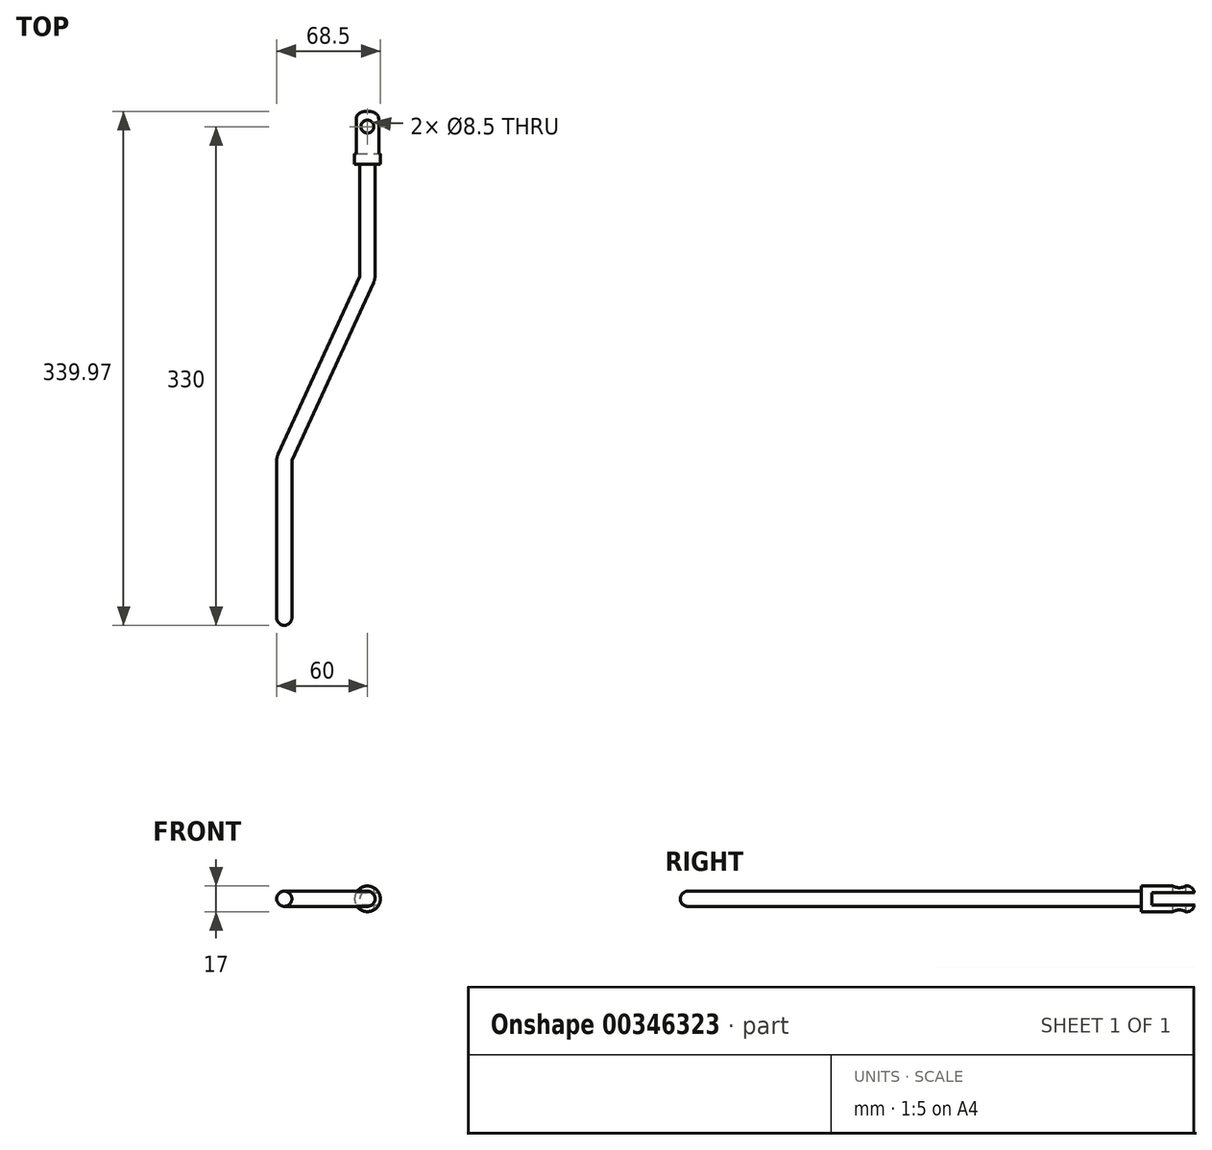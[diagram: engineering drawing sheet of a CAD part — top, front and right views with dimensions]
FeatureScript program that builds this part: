
annotation { "Feature Type Name" : "Feature", "Feature Type Description" : "" }
export const myFeature = defineFeature(function(context is Context, id is Id, definition is map)
    precondition{}
    {
        {
            var Q0;
            Q0=qCreatedBy(makeId("Top.planeOp"),FACE);
            var sketch = newSketch(context, id + "F0", { "sketchPlane" : qUnion([Q0])});
            skLineSegment(sketch, "E0.bottom", {"start": v(-3.5, 0) * mm, "end": v(3.5, 0) * mm});
            skLineSegment(sketch, "E0.top", {"start": v(-8.5, -35) * mm, "end": v(8.5, -35) * mm});
            skLineSegment(sketch, "E0.left", {"start": v(-8.5, -5) * mm, "end": v(-8.5, -35) * mm});
            skLineSegment(sketch, "E0.right", {"start": v(8.5, -5) * mm, "end": v(8.5, -35) * mm});
            skPoint(sketch, "E1.visualSharp", {"position": v(-8.5, 0) * mm});
            skArc(sketch, "E1.filletArc", {"start": v(-3.5, 0) * mm, "mid": v(-7.04, -1.46) * mm, "end": v(-8.5, -5) * mm});
            skPoint(sketch, "E2.visualSharp", {"position": v(8.5, 0) * mm});
            skArc(sketch, "E2.filletArc", {"start": v(8.5, -5) * mm, "mid": v(7.04, -1.46) * mm, "end": v(3.5, 0) * mm});
            skLineSegment(sketch, "E3", {"start": v(0, 6.79) * mm, "end": v(0, 0) * mm, "construction": true});
            skCircle(sketch, "E4", {"center": v(0, -10) * mm, "radius": 4.25 * mm});
            skLineSegment(sketch, "E5", {"start": v(0, -35) * mm, "end": v(0, -108.7) * mm});
            skLineSegment(sketch, "E6", {"start": v(-0.55, -111.2) * mm, "end": v(-54.45, -228.8) * mm});
            skLineSegment(sketch, "E7", {"start": v(-55, -231.3) * mm, "end": v(-55, -340) * mm});
            skLineSegment(sketch, "E8", {"start": v(0, 0) * mm, "end": v(0, -35) * mm});
            skPoint(sketch, "E9.visualSharp", {"position": v(0, -110) * mm});
            skArc(sketch, "E9.filletArc", {"start": v(-0.55, -111.2) * mm, "mid": v(-0.14, -109.97) * mm, "end": v(0, -108.7) * mm});
            skPoint(sketch, "E10.visualSharp", {"position": v(-55, -230) * mm});
            skArc(sketch, "E10.filletArc", {"start": v(-54.45, -228.8) * mm, "mid": v(-54.86, -230.03) * mm, "end": v(-55, -231.3) * mm});
            skSolve(sketch);
        }
        {
            var Q0;
            {var subQ1=sQuery(id+"F0.wireOp",EDGE,"E0.left");Q0=makeQuery(id+"F0.imprint","IMPRINT",FACE,{"disambiguationData":[TD([[makeQuery(id+"F0.imprint","IMPRINT",EDGE,{"derivedFrom":subQ1}),1.0]])]});}
            var Q1;
            {var subQ0=sQuery(id+"F0.wireOp",EDGE,"E8");var subQ1=sQuery(id+"F0.wireOp",EDGE,"E4");var subQ2=makeQuery(id+"F0.imprint","INTERSECT",VERTEX,{"disambiguationData":[OD(0.0)],"derivedFrom":[subQ1,subQ0]});Q1=makeQuery(id+"F0.imprint","IMPRINT",FACE,{"disambiguationData":[TD([[makeQuery(id+"F0.imprint","IMPRINT",EDGE,{"disambiguationData":[TD([[subQ2,-1.0]])],"derivedFrom":subQ1}),1.0]])]});}
            var Q2;
            Q2=sQuery(id+"F0.wireOp",EDGE,"E8");
            revolve(context, id + "F1", {"entities" : qUnion([Q0, Q1]), "axis" : qUnion([Q2]), "revolveType" : RevolveType.FULL});
        }
        {
            var Q0;
            {var subQ0=sQuery(id+"F0.wireOp",EDGE,"E8");var subQ1=sQuery(id+"F0.wireOp",EDGE,"E4");var subQ2=makeQuery(id+"F0.imprint","INTERSECT",VERTEX,{"disambiguationData":[OD(0.0)],"derivedFrom":[subQ1,subQ0]});Q0=makeQuery(id+"F0.imprint","IMPRINT",FACE,{"disambiguationData":[TD([[makeQuery(id+"F0.imprint","IMPRINT",EDGE,{"disambiguationData":[TD([[subQ2,-1.0]])],"derivedFrom":subQ1}),1.0]])]});}
            var Q1;
            {var subQ0=sQuery(id+"F0.wireOp",EDGE,"E8");var subQ1=sQuery(id+"F0.wireOp",EDGE,"E4");var subQ2=makeQuery(id+"F0.imprint","INTERSECT",VERTEX,{"disambiguationData":[OD(0.0)],"derivedFrom":[subQ1,subQ0]});Q1=makeQuery(id+"F0.imprint","IMPRINT",FACE,{"disambiguationData":[TD([[makeQuery(id+"F0.imprint","IMPRINT",EDGE,{"disambiguationData":[TD([[subQ2,1.0]])],"derivedFrom":subQ1}),1.0]])]});}
            extrude(context, id + "F2", {"entities" : qUnion([Q0, Q1]), "operationType" : NewBodyOperationType.REMOVE, "oppositeDirection" : true, "depth" : 25 * mm, "hasSecondDirection" : true, "secondDirectionOppositeDirection" : false, "secondDirectionDepth" : 25 * mm});
        }
        {
            var Q0;
            Q0=qCreatedBy(makeId("Right.planeOp"),FACE);
            var sketch = newSketch(context, id + "F3", { "sketchPlane" : qUnion([Q0])});
            skLineSegment(sketch, "E11.bottom", {"start": v(28, 4) * mm, "end": v(-28, 4) * mm});
            skLineSegment(sketch, "E11.top", {"start": v(28, -4) * mm, "end": v(-28, -4) * mm});
            skLineSegment(sketch, "E11.left", {"start": v(28, 4) * mm, "end": v(28, -4) * mm});
            skLineSegment(sketch, "E11.right", {"start": v(-28, 4) * mm, "end": v(-28, -4) * mm});
            skPoint(sketch, "E11.middle", {"position": v(0, 0) * mm});
            skSolve(sketch);
        }
        {
            var Q0;
            Q0=makeQuery(id+"F3.imprint","IMPRINT",FACE,{"disambiguationData":[TD([[makeQuery(id+"F3.imprint","IMPRINT",EDGE,{"derivedFrom":sQuery(id+"F3.wireOp",EDGE,"E11.bottom")}),1.0]])]});
            extrude(context, id + "F4", {"entities" : qUnion([Q0]), "operationType" : NewBodyOperationType.REMOVE, "oppositeDirection" : true, "depth" : 25 * mm, "hasSecondDirection" : true, "secondDirectionOppositeDirection" : false, "secondDirectionDepth" : 25 * mm});
        }
        {
            var Q0;
            Q0=makeQuery(id+"F1.opRevolve","SWEPT_FACE",FACE,{"disambiguationData":[OSD([sQuery(id+"F0.wireOp",EDGE,"E0.top")])]});
            var sketch = newSketch(context, id + "F5", { "sketchPlane" : qUnion([Q0])});
            skCircle(sketch, "E12", {"center": v(0, 0) * mm, "radius": 5 * mm});
            skSolve(sketch);
        }
        {
            var Q0;
            Q0=makeQuery(id+"F5.imprint","IMPRINT",FACE,{"disambiguationData":[TD([[makeQuery(id+"F5.imprint","IMPRINT",EDGE,{"derivedFrom":sQuery(id+"F5.wireOp",EDGE,"E12")}),1.0]])]});
            var Q1;
            Q1=sQuery(id+"F0.wireOp",EDGE,"E5");
            var Q2;
            Q2=sQuery(id+"F0.wireOp",EDGE,"E6");
            var Q3;
            Q3=sQuery(id+"F0.wireOp",EDGE,"E7");
            var Q4;
            Q4=sQuery(id+"F0.wireOp",EDGE,"E9.filletArc");
            var Q5;
            Q5=sQuery(id+"F0.wireOp",EDGE,"E10.filletArc");
            sweep(context, id + "F6", {"operationType" : NewBodyOperationType.ADD, "profiles" : qUnion([Q0]), "path" : qUnion([Q1, Q2, Q3, Q4, Q5])});
        }
        {
            var Q0;
            Q0=makeQuery(id+"F6.opSweep","CAP_EDGE",EDGE,{"disambiguationData":[OSD([sQuery(id+"F0.wireOp",VERTEX,"E7.end"),sQuery(id+"F5.wireOp",EDGE,"E12")])],"isStart":false});
            fillet(context, id + "F7", {"entities" : qUnion([Q0]), "radius" : 5 * mm, "tangentPropagation" : true, "allowEdgeOverflow" : false});
        }
    });
